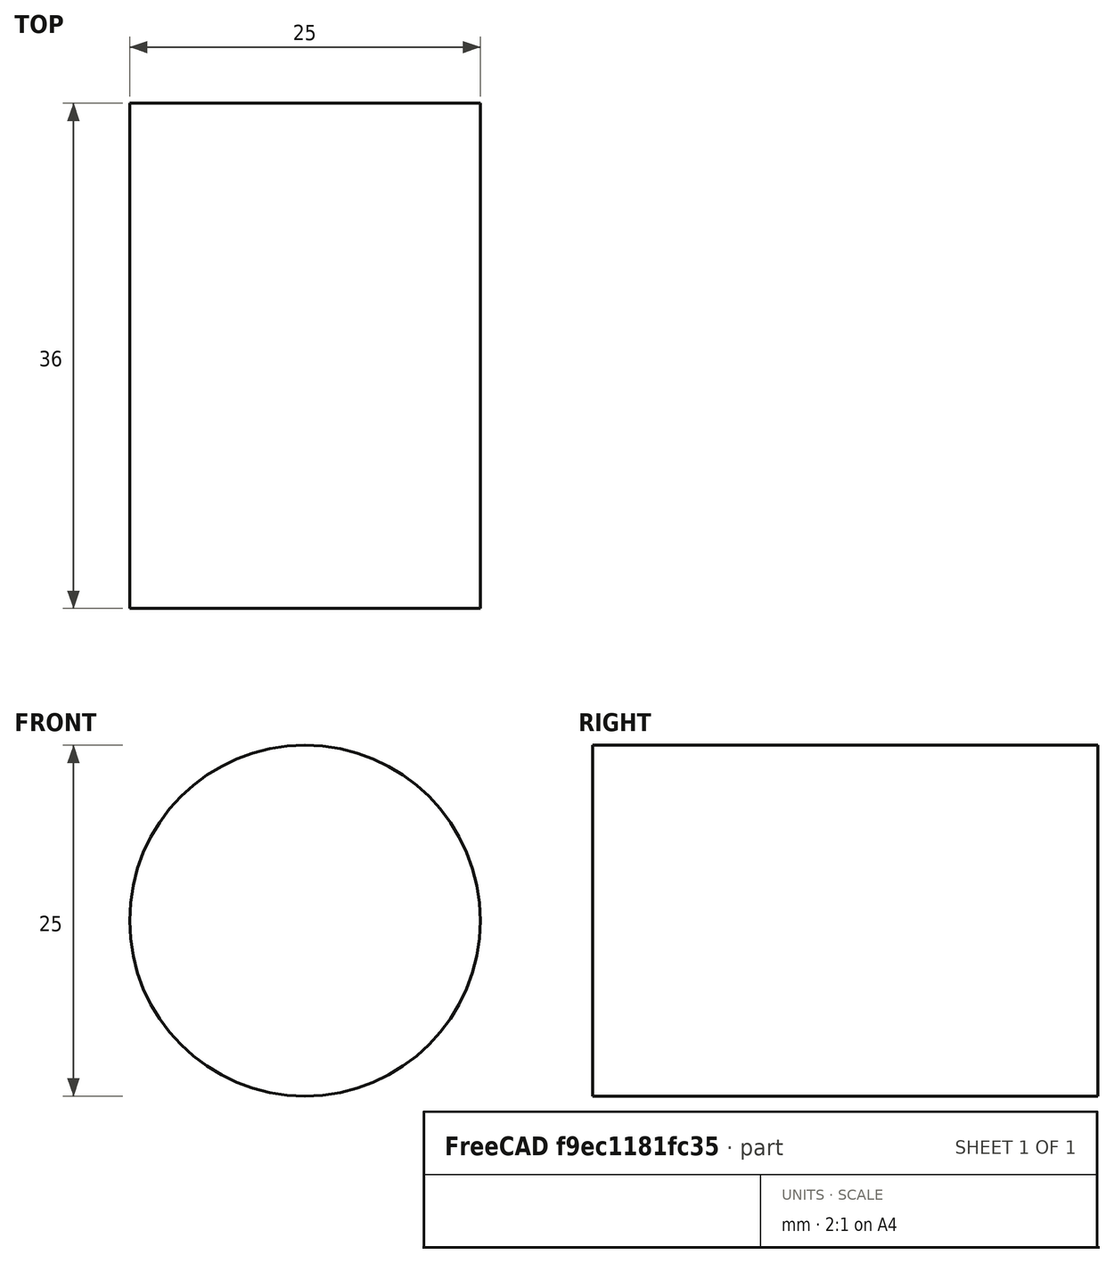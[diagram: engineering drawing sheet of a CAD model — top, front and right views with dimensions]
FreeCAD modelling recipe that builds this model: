
FCSTD DOCUMENT  (FreeCAD 0.19R24291 (Git))
Label: whiteBoardLegs
License: All rights reserved
LicenseURL: http://en.wikipedia.org/wiki/All_rights_reserved
objects: Sketcher::SketchObject×1, PartDesign::Pad×1, PartDesign::Body×1
note: 4 computed .brp shape members not serialized (recipe doc carries the construction recipe); baked Part::Feature solids carry a one-line shape summary decoded from their .brp

FEATURE [Sketcher::SketchObject] Sketch
  FullyConstrained = true
  MapMode = 5
  Placement = pos=(0,0,0) rot=(1,0,0;1.5708rad)
  Support = -> [XZ_Plane]
  sketch-geometry (1):
    g0: Circle CenterX=0 CenterY=0 CenterZ=0 NormalX=0 NormalY=0 NormalZ=1 AngleXU=0 Radius=12.5
  constraints (2):
    c: Coincident(g0,g-1)
    c: Diameter(g0) = 25
FEATURE [PartDesign::Pad] Pad
  Direction = (1,1,1)
  Length = 36
  Length2 = 100
  Placement = pos=(0,0,0) rot=(1,0,0;1.5708rad)
  Profile = -> Sketch
  Type = 0
FEATURE [PartDesign::Body] Body
  Group = -> [Sketch,Pad]
  Origin = -> Origin
  Tip = -> Pad
